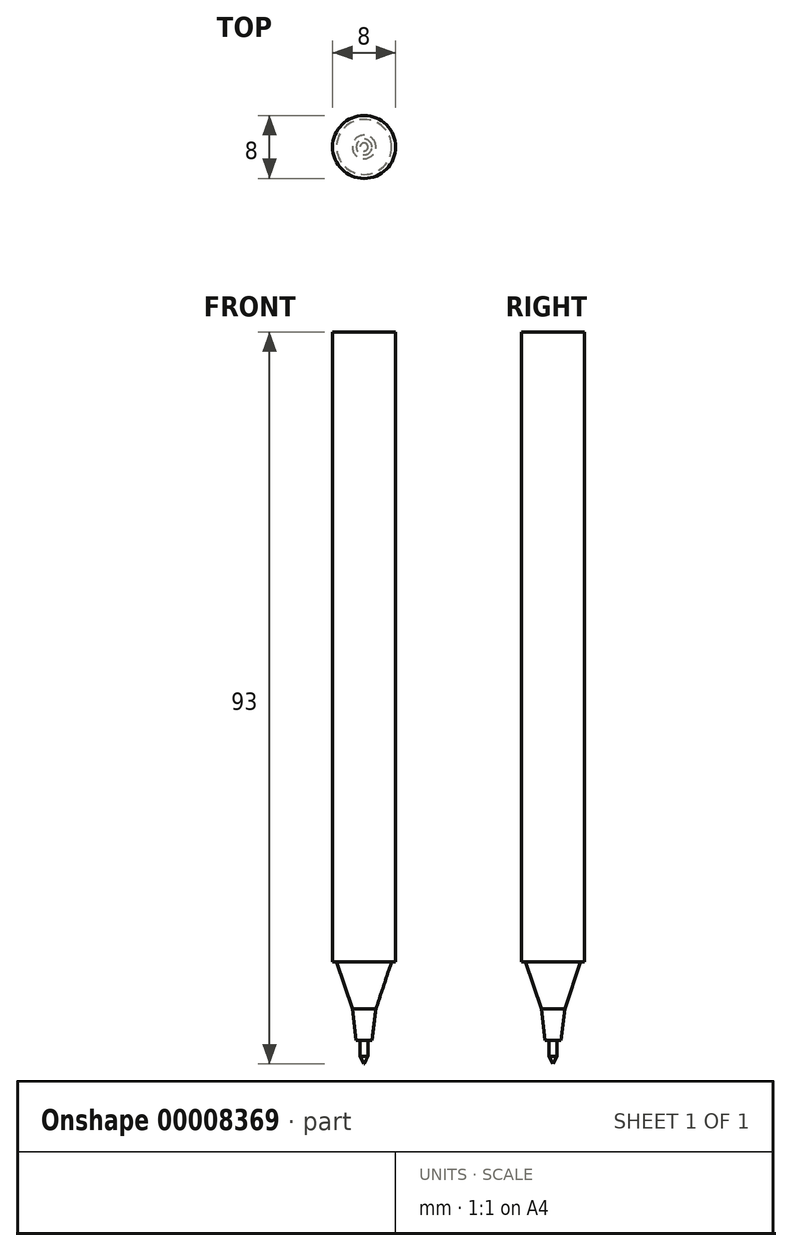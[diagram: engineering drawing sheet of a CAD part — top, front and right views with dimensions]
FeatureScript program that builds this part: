
annotation { "Feature Type Name" : "Feature", "Feature Type Description" : "" }
export const myFeature = defineFeature(function(context is Context, id is Id, definition is map)
    precondition{}
    {
        {
            var Q0;
            Q0=qCreatedBy(makeId("Front.planeOp"),FACE);
            var sketch = newSketch(context, id + "F0", { "sketchPlane" : qUnion([Q0])});
            skLineSegment(sketch, "E0", {"start": v(0, 0) * mm, "end": v(0.5, 1) * mm});
            skLineSegment(sketch, "E1", {"start": v(0.5, 1) * mm, "end": v(0.5, 3) * mm});
            skLineSegment(sketch, "E2", {"start": v(0.5, 3) * mm, "end": v(1, 3) * mm});
            skLineSegment(sketch, "E3", {"start": v(1, 3) * mm, "end": v(1.5, 7) * mm});
            skLineSegment(sketch, "E4", {"start": v(1.5, 7) * mm, "end": v(3.5, 13) * mm});
            skLineSegment(sketch, "E5", {"start": v(3.5, 13) * mm, "end": v(4, 13) * mm});
            skLineSegment(sketch, "E6", {"start": v(4, 13) * mm, "end": v(4, 93) * mm});
            skLineSegment(sketch, "E7", {"start": v(4, 93) * mm, "end": v(0, 93) * mm});
            skLineSegment(sketch, "E8", {"start": v(0, 93) * mm, "end": v(0, 0) * mm});
            skSolve(sketch);
        }
        {
            var Q0;
            Q0 = qSketchRegion(id + "F0", true);
            var Q1;
            Q1=sQuery(id+"F0.wireOp",EDGE,"E8");
            revolve(context, id + "F1", {"entities" : qUnion([Q0]), "axis" : qUnion([Q1]), "revolveType" : RevolveType.FULL});
        }
    });
